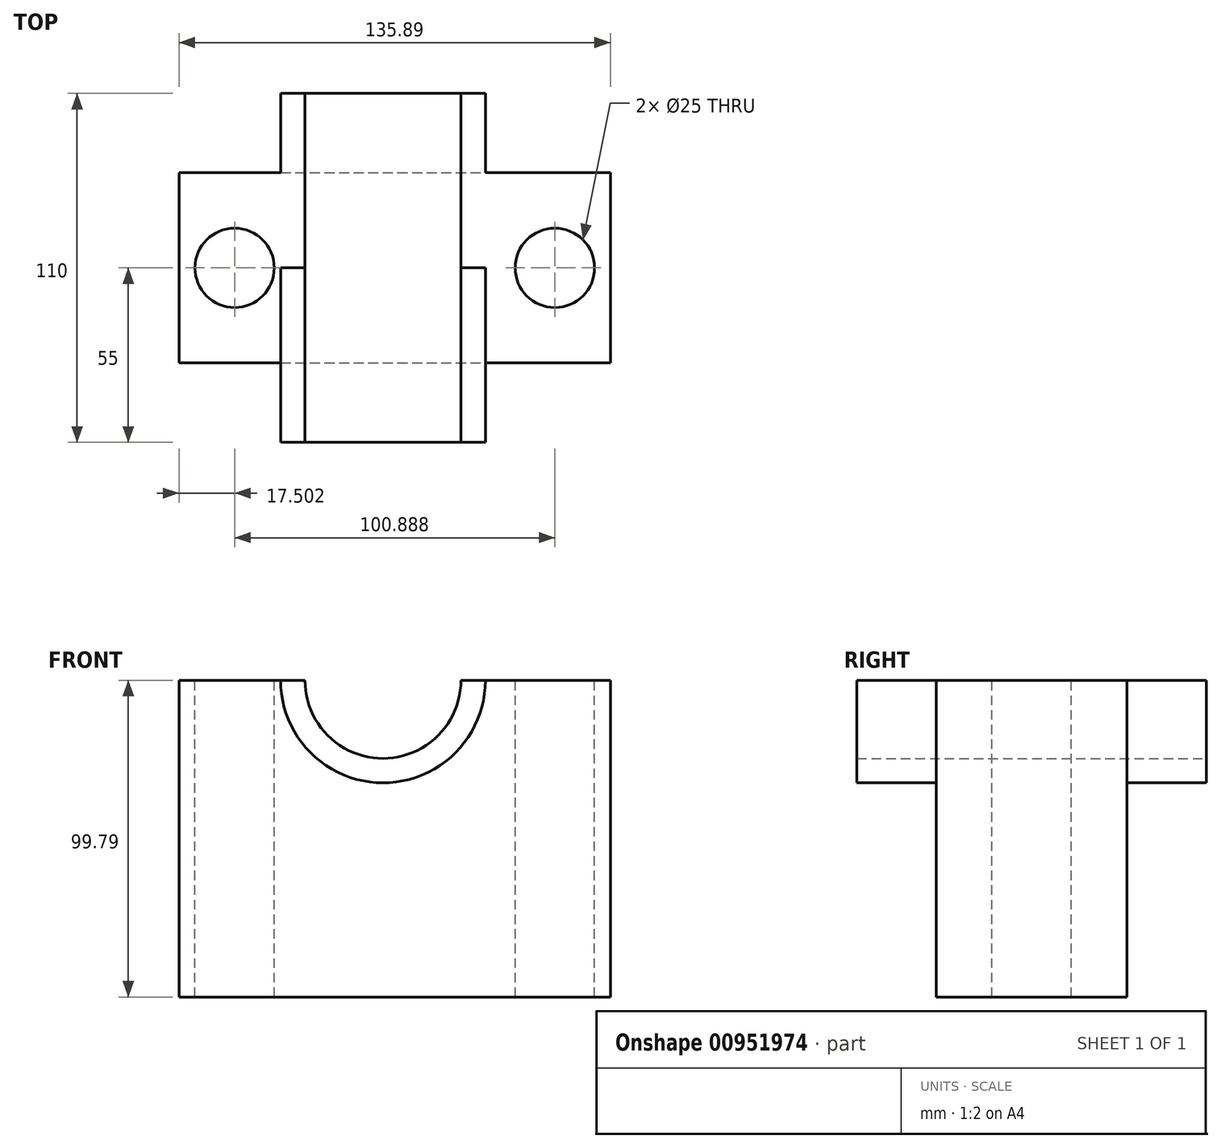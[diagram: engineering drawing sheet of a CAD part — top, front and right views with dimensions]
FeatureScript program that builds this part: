
annotation { "Feature Type Name" : "Feature", "Feature Type Description" : "" }
export const myFeature = defineFeature(function(context is Context, id is Id, definition is map)
    precondition{}
    {
        {
            var Q0;
            Q0=qCreatedBy(makeId("Front.planeOp"),FACE);
            var sketch = newSketch(context, id + "F0", { "sketchPlane" : qUnion([Q0])});
            skLineSegment(sketch, "E0.bottom", {"start": v(-67.65, 49.88) * mm, "end": v(68.24, 49.88) * mm});
            skLineSegment(sketch, "E0.top", {"start": v(-67.65, -49.88) * mm, "end": v(68.24, -49.88) * mm});
            skLineSegment(sketch, "E0.left", {"start": v(-67.65, 49.88) * mm, "end": v(-67.65, -49.88) * mm});
            skLineSegment(sketch, "E0.right", {"start": v(68.24, 49.88) * mm, "end": v(68.24, -49.88) * mm});
            skSolve(sketch);
        }
        {
            var Q0;
            Q0=makeQuery(id+"F0.imprint","IMPRINT",FACE,{"disambiguationData":[TD([[makeQuery(id+"F0.imprint","IMPRINT",EDGE,{"derivedFrom":sQuery(id+"F0.wireOp",EDGE,"E0.bottom")}),-1.0]])]});
            var sketch = newSketch(context, id + "F1", { "sketchPlane" : qUnion([Q0])});
            skCircle(sketch, "E1", {"center": v(-3.4, 49.88) * mm, "radius": 32.26 * mm});
            skCircle(sketch, "E2", {"center": v(-3.4, 49.88) * mm, "radius": 24.57 * mm});
            skSolve(sketch);
        }
        {
            var Q0;
            Q0=makeQuery(id+"F1.imprint","IMPRINT",FACE,{"disambiguationData":[TD([[makeQuery(id+"F1.imprint","IMPRINT",EDGE,{"derivedFrom":makeQuery(id+"F0.imprint","IMPRINT",EDGE,{"derivedFrom":sQuery(id+"F0.wireOp",EDGE,"E0.top")})}),1.0]])]});
            extrude(context, id + "F2", {"entities" : qUnion([Q0]), "depth" : 30 * mm, "offsetDistance" : 25 * mm});
        }
        {
            var Q0;
            Q0=makeQuery(id+"F2.opExtrude","SWEPT_BODY",BODY,{"disambiguationData":[OSD([sQuery(id+"F0.wireOp",EDGE,"E0.bottom"),sQuery(id+"F0.wireOp",EDGE,"E0.top"),sQuery(id+"F0.wireOp",EDGE,"E0.left"),sQuery(id+"F0.wireOp",EDGE,"E0.right"),sQuery(id+"F1.wireOp",EDGE,"E1")])]});
            var Q1;
            Q1=makeQuery(id+"F0.imprint","IMPRINT",FACE,{"disambiguationData":[TD([[makeQuery(id+"F0.imprint","IMPRINT",EDGE,{"derivedFrom":sQuery(id+"F0.wireOp",EDGE,"E0.bottom")}),-1.0]])]});
            mirror(context, id + "F3", {"operationType" : NewBodyOperationType.ADD, "entities" : qUnion([Q0]), "mirrorPlane" : qUnion([Q1])});
        }
        {
            var Q0;
            Q0 = qSketchRegion(id + "F1", true);
            extrude(context, id + "F4", {"entities" : qUnion([Q0]), "operationType" : NewBodyOperationType.ADD, "depth" : 55 * mm, "offsetDistance" : 25 * mm});
        }
        {
            var Q0;
            Q0=makeQuery(id+"F2.opExtrude","SWEPT_BODY",BODY,{"disambiguationData":[OSD([sQuery(id+"F0.wireOp",EDGE,"E0.bottom"),sQuery(id+"F0.wireOp",EDGE,"E0.top"),sQuery(id+"F0.wireOp",EDGE,"E0.left"),sQuery(id+"F0.wireOp",EDGE,"E0.right"),sQuery(id+"F1.wireOp",EDGE,"E1")])]});
            var Q1;
            {var subQ0=sQuery(id+"F1.wireOp",EDGE,"E1");var subQ1=makeQuery(id+"F0.imprint","IMPRINT",EDGE,{"derivedFrom":sQuery(id+"F0.wireOp",EDGE,"E0.bottom")});var subQ2=makeQuery(id+"F1.imprint","INTERSECT",VERTEX,{"disambiguationData":[OD(0.0)],"derivedFrom":[subQ1,subQ0]});Q1=makeQuery(id+"F1.imprint","IMPRINT",FACE,{"disambiguationData":[TD([[makeQuery(id+"F1.imprint","IMPRINT",EDGE,{"disambiguationData":[TD([[subQ2,1.0]])],"derivedFrom":subQ0}),1.0]])]});}
            mirror(context, id + "F5", {"operationType" : NewBodyOperationType.ADD, "entities" : qUnion([Q0]), "mirrorPlane" : qUnion([Q1])});
        }
        {
            var Q0;
            Q0=qCreatedBy(makeId("Front.planeOp"),FACE);
            var sketch = newSketch(context, id + "F6", { "sketchPlane" : qUnion([Q0])});
            skLineSegment(sketch, "E3.bottom", {"start": v(-35.7, 49.88) * mm, "end": v(30.2, 49.88) * mm});
            skLineSegment(sketch, "E3.top", {"start": v(-35.7, 83) * mm, "end": v(30.2, 83) * mm});
            skLineSegment(sketch, "E3.left", {"start": v(-35.7, 49.88) * mm, "end": v(-35.7, 83) * mm});
            skLineSegment(sketch, "E3.right", {"start": v(30.2, 49.88) * mm, "end": v(30.2, 83) * mm});
            skSolve(sketch);
        }
        {
            var Q0;
            Q0=makeQuery(id+"F6.imprint","IMPRINT",FACE,{"disambiguationData":[TD([[makeQuery(id+"F6.imprint","IMPRINT",EDGE,{"derivedFrom":sQuery(id+"F6.wireOp",EDGE,"E3.bottom")}),1.0]])]});
            extrude(context, id + "F7", {"entities" : qUnion([Q0]), "operationType" : NewBodyOperationType.REMOVE, "oppositeDirection" : true, "depth" : 55 * mm, "offsetDistance" : 25 * mm});
        }
        {
            var Q0;
            Q0=qCreatedBy(makeId("Front.planeOp"),FACE);
            var sketch = newSketch(context, id + "F8", { "sketchPlane" : qUnion([Q0])});
            skLineSegment(sketch, "E4.bottom", {"start": v(29.08, 49.91) * mm, "end": v(-36.75, 49.91) * mm});
            skLineSegment(sketch, "E4.top", {"start": v(29.08, 85.61) * mm, "end": v(-36.75, 85.61) * mm});
            skLineSegment(sketch, "E4.left", {"start": v(29.08, 49.91) * mm, "end": v(29.08, 85.61) * mm});
            skLineSegment(sketch, "E4.right", {"start": v(-36.75, 49.91) * mm, "end": v(-36.75, 85.61) * mm});
            skSolve(sketch);
        }
        {
            var Q0;
            Q0=makeQuery(id+"F8.imprint","IMPRINT",FACE,{"disambiguationData":[TD([[makeQuery(id+"F8.imprint","IMPRINT",EDGE,{"derivedFrom":sQuery(id+"F8.wireOp",EDGE,"E4.bottom")}),-1.0]])]});
            extrude(context, id + "F9", {"entities" : qUnion([Q0]), "operationType" : NewBodyOperationType.REMOVE, "depth" : 55 * mm, "offsetDistance" : 25 * mm});
        }
        {
            var Q0;
            {var subQ0=sQuery(id+"F0.wireOp",EDGE,"E0.bottom");var subQ1=makeQuery(id+"F0.imprint","IMPRINT",EDGE,{"derivedFrom":subQ0});var subQ2=makeQuery(id+"F2.opExtrude","SWEPT_FACE",FACE,{"disambiguationData":[OSD([subQ0]),TDD([makeQuery(id+"F1.imprint","IMPRINT",EDGE,{"disambiguationData":[TD([[makeQuery(id+"F1.imprint","INTERSECT",VERTEX,{"derivedFrom":[subQ1,makeQuery(id+"F0.imprint","IMPRINT",EDGE,{"derivedFrom":sQuery(id+"F0.wireOp",EDGE,"E0.left")})]}),-1.0]])],"derivedFrom":subQ1})])]});Q0=makeQuery(id+"F3.boolean.opBoolean","MERGE",FACE,{"derivedFrom":[subQ2,makeQuery(id+"F3.opPattern","COPY",FACE,{"derivedFrom":subQ2,"instanceName":"1"})]});}
            var sketch = newSketch(context, id + "F10", { "sketchPlane" : qUnion([Q0])});
            skCircle(sketch, "E5", {"center": v(-50.15, 0) * mm, "radius": 12.5 * mm});
            skSolve(sketch);
        }
        {
            var Q0;
            Q0=makeQuery(id+"F10.imprint","IMPRINT",FACE,{"disambiguationData":[TD([[makeQuery(id+"F10.imprint","IMPRINT",EDGE,{"derivedFrom":sQuery(id+"F10.wireOp",EDGE,"E5")}),1.0]])]});
            extrude(context, id + "F11", {"entities" : qUnion([Q0]), "operationType" : NewBodyOperationType.REMOVE, "oppositeDirection" : true, "depth" : 100 * mm, "offsetDistance" : 25 * mm});
        }
        {
            var Q0;
            {var subQ0=sQuery(id+"F0.wireOp",EDGE,"E0.bottom");var subQ1=makeQuery(id+"F0.imprint","IMPRINT",EDGE,{"derivedFrom":subQ0});var subQ2=makeQuery(id+"F2.opExtrude","SWEPT_FACE",FACE,{"disambiguationData":[OSD([subQ0]),TDD([makeQuery(id+"F1.imprint","IMPRINT",EDGE,{"disambiguationData":[TD([[makeQuery(id+"F1.imprint","INTERSECT",VERTEX,{"derivedFrom":[subQ1,makeQuery(id+"F0.imprint","IMPRINT",EDGE,{"derivedFrom":sQuery(id+"F0.wireOp",EDGE,"E0.right")})]}),1.0]])],"derivedFrom":subQ1})])]});Q0=makeQuery(id+"F3.boolean.opBoolean","MERGE",FACE,{"derivedFrom":[subQ2,makeQuery(id+"F3.opPattern","COPY",FACE,{"derivedFrom":subQ2,"instanceName":"1"})]});}
            var sketch = newSketch(context, id + "F12", { "sketchPlane" : qUnion([Q0])});
            skCircle(sketch, "E6", {"center": v(50.74, 0) * mm, "radius": 12.5 * mm});
            skSolve(sketch);
        }
        {
            var Q0;
            Q0=makeQuery(id+"F12.imprint","IMPRINT",FACE,{"disambiguationData":[TD([[makeQuery(id+"F12.imprint","IMPRINT",EDGE,{"derivedFrom":sQuery(id+"F12.wireOp",EDGE,"E6")}),1.0]])]});
            extrude(context, id + "F13", {"entities" : qUnion([Q0]), "operationType" : NewBodyOperationType.REMOVE, "oppositeDirection" : true, "depth" : 100 * mm, "offsetDistance" : 25 * mm});
        }
    });
